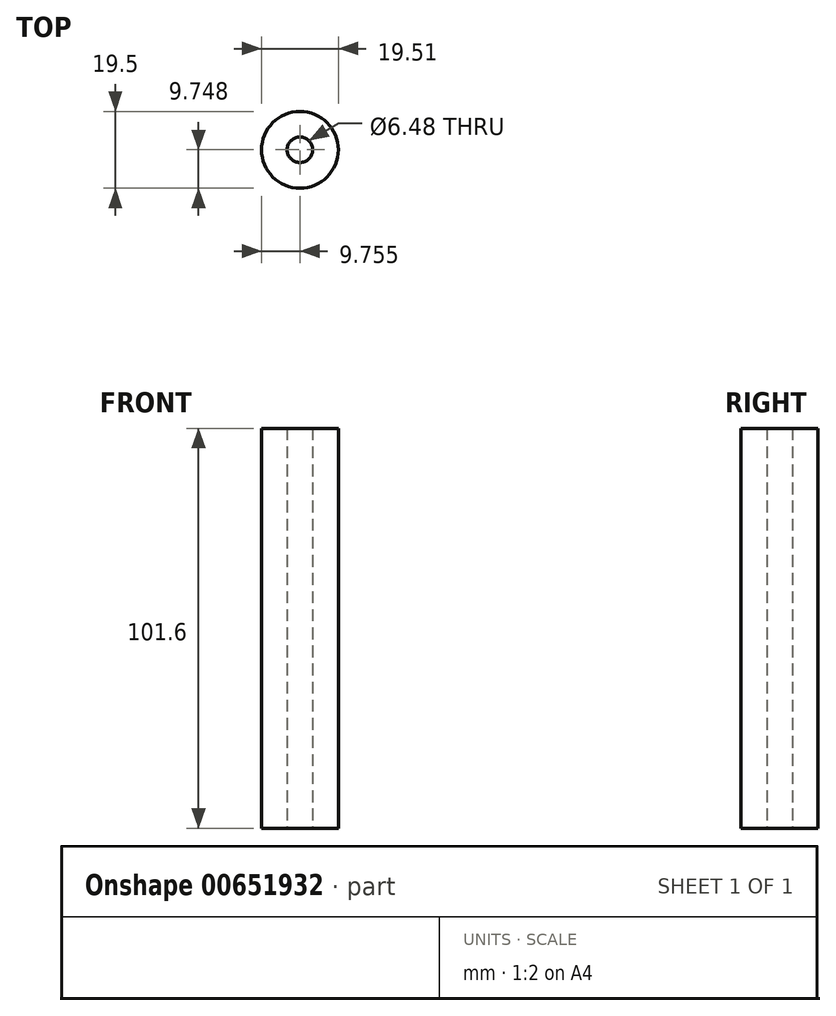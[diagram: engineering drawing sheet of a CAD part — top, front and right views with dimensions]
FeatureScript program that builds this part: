
annotation { "Feature Type Name" : "Feature", "Feature Type Description" : "" }
export const myFeature = defineFeature(function(context is Context, id is Id, definition is map)
    precondition{}
    {
        {
            var Q0;
            Q0=qCreatedBy(makeId("Top.planeOp"),FACE);
            var sketch = newSketch(context, id + "F0", { "sketchPlane" : qUnion([Q0])});
            skCircle(sketch, "E0", {"center": v(-35.48, 44.19) * mm, "radius": 9.75 * mm});
            skCircle(sketch, "E1", {"center": v(-35.48, 44.19) * mm, "radius": 3.24 * mm});
            skSolve(sketch);
        }
        {
            var Q0;
            Q0=makeQuery(id+"F0.imprint","IMPRINT",FACE,{"disambiguationData":[TD([[makeQuery(id+"F0.imprint","IMPRINT",EDGE,{"derivedFrom":sQuery(id+"F0.wireOp",EDGE,"E0")}),1.0]])]});
            extrude(context, id + "F1", {"entities" : qUnion([Q0]), "endBound" : BoundingType.SYMMETRIC, "depth" : 101.6 * mm, "offsetDistance" : 25.4 * mm});
        }
    });
